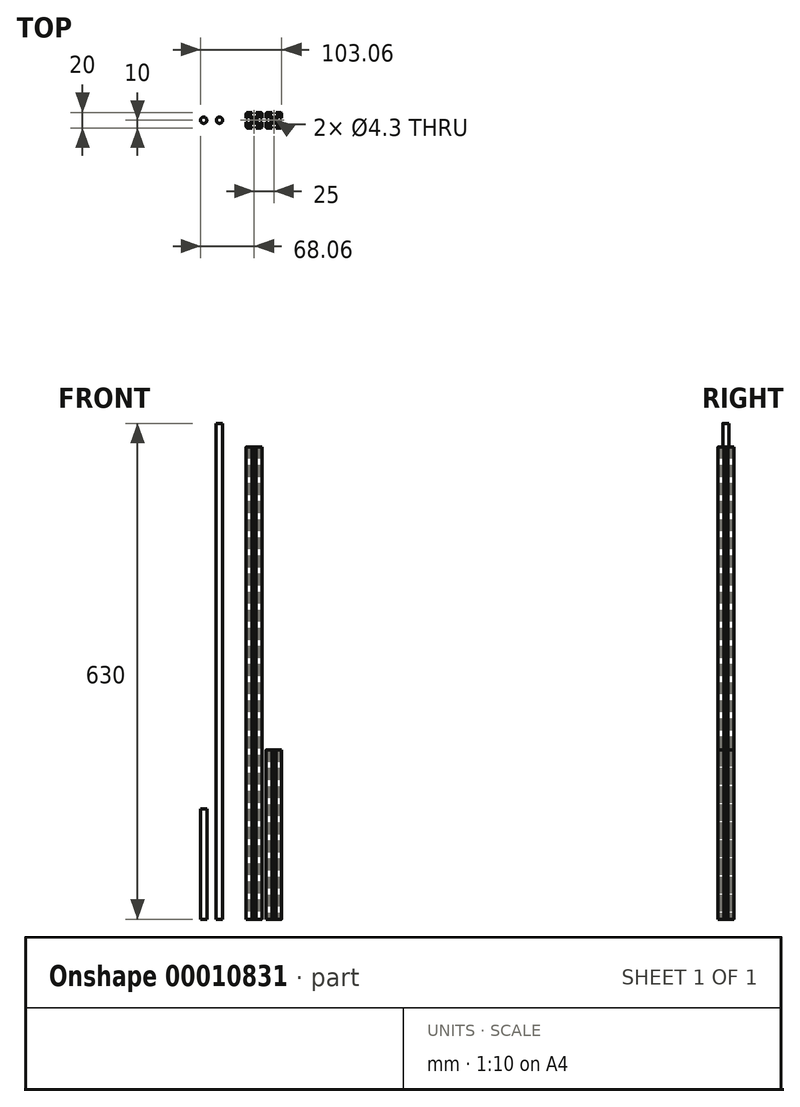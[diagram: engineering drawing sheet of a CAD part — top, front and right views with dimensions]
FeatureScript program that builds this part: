
annotation { "Feature Type Name" : "Feature", "Feature Type Description" : "" }
export const myFeature = defineFeature(function(context is Context, id is Id, definition is map)
    precondition{}
    {
        {
            var Q0;
            Q0=qCreatedBy(makeId("Top.planeOp"),FACE);
            var sketch = newSketch(context, id + "F0", { "sketchPlane" : qUnion([Q0])});
            skLineSegment(sketch, "E0.rect.bottom", {"start": v(8, 10) * mm, "end": v(-8, 10) * mm});
            skLineSegment(sketch, "E0.rect.top", {"start": v(8, -10) * mm, "end": v(-8, -10) * mm});
            skLineSegment(sketch, "E0.rect.left", {"start": v(10, 8) * mm, "end": v(10, -8) * mm});
            skLineSegment(sketch, "E0.rect.right", {"start": v(-10, 8) * mm, "end": v(-10, -8) * mm});
            skPoint(sketch, "E0.rect.middle", {"position": v(0, 0) * mm});
            skPoint(sketch, "E1.visualSharp", {"position": v(-10, 10) * mm});
            skArc(sketch, "E1.filletArc", {"start": v(-8, 10) * mm, "mid": v(-9.41, 9.41) * mm, "end": v(-10, 8) * mm});
            skPoint(sketch, "E2.visualSharp", {"position": v(10, 10) * mm});
            skArc(sketch, "E2.filletArc", {"start": v(10, 8) * mm, "mid": v(9.41, 9.41) * mm, "end": v(8, 10) * mm});
            skPoint(sketch, "E3.visualSharp", {"position": v(10, -10) * mm});
            skArc(sketch, "E3.filletArc", {"start": v(8, -10) * mm, "mid": v(9.41, -9.41) * mm, "end": v(10, -8) * mm});
            skPoint(sketch, "E4.visualSharp", {"position": v(-10, -10) * mm});
            skArc(sketch, "E4.filletArc", {"start": v(-10, -8) * mm, "mid": v(-9.41, -9.41) * mm, "end": v(-8, -10) * mm});
            skCircle(sketch, "E5", {"center": v(0, 0) * mm, "radius": 2.15 * mm});
            skCircle(sketch, "E6", {"center": v(0, 0) * mm, "radius": 3.65 * mm});
            skLineSegment(sketch, "E7", {"start": v(-2.5, 10) * mm, "end": v(-2.5, 8.2) * mm});
            skLineSegment(sketch, "E8", {"start": v(-2.5, 8.2) * mm, "end": v(-5.7, 8.2) * mm});
            skLineSegment(sketch, "E9", {"start": v(-5.7, 8.2) * mm, "end": v(-5.7, 7) * mm});
            skLineSegment(sketch, "E10", {"start": v(-5.7, 7) * mm, "end": v(-1.85, 3.15) * mm});
            skLineSegment(sketch, "E11", {"start": v(0, 16.28) * mm, "end": v(0, -16.6) * mm, "construction": true});
            skLineSegment(sketch, "E12", {"start": v(2.5, 10) * mm, "end": v(2.5, 8.2) * mm});
            skLineSegment(sketch, "E13", {"start": v(2.5, 8.2) * mm, "end": v(5.7, 8.2) * mm});
            skLineSegment(sketch, "E14", {"start": v(5.7, 8.2) * mm, "end": v(5.7, 7) * mm});
            skLineSegment(sketch, "E15", {"start": v(5.7, 7) * mm, "end": v(1.85, 3.15) * mm});
            skLineSegment(sketch, "E16.1.0", {"start": v(-7, -5.7) * mm, "end": v(-3.15, -1.85) * mm});
            skLineSegment(sketch, "E16.1.1", {"start": v(-8.2, -5.7) * mm, "end": v(-7, -5.7) * mm});
            skLineSegment(sketch, "E16.1.2", {"start": v(-8.2, -2.5) * mm, "end": v(-8.2, -5.7) * mm});
            skLineSegment(sketch, "E16.1.3", {"start": v(-10, -2.5) * mm, "end": v(-8.2, -2.5) * mm});
            skLineSegment(sketch, "E16.1.4", {"start": v(-10, 2.5) * mm, "end": v(-8.2, 2.5) * mm});
            skLineSegment(sketch, "E16.1.5", {"start": v(-8.2, 2.5) * mm, "end": v(-8.2, 5.7) * mm});
            skLineSegment(sketch, "E16.1.6", {"start": v(-8.2, 5.7) * mm, "end": v(-7, 5.7) * mm});
            skLineSegment(sketch, "E16.1.7", {"start": v(-7, 5.7) * mm, "end": v(-3.15, 1.85) * mm});
            skLineSegment(sketch, "E16.2.0", {"start": v(5.7, -7) * mm, "end": v(1.85, -3.15) * mm});
            skLineSegment(sketch, "E16.2.1", {"start": v(5.7, -8.2) * mm, "end": v(5.7, -7) * mm});
            skLineSegment(sketch, "E16.2.2", {"start": v(2.5, -8.2) * mm, "end": v(5.7, -8.2) * mm});
            skLineSegment(sketch, "E16.2.3", {"start": v(2.5, -10) * mm, "end": v(2.5, -8.2) * mm});
            skLineSegment(sketch, "E16.2.4", {"start": v(-2.5, -10) * mm, "end": v(-2.5, -8.2) * mm});
            skLineSegment(sketch, "E16.2.5", {"start": v(-2.5, -8.2) * mm, "end": v(-5.7, -8.2) * mm});
            skLineSegment(sketch, "E16.2.6", {"start": v(-5.7, -8.2) * mm, "end": v(-5.7, -7) * mm});
            skLineSegment(sketch, "E16.2.7", {"start": v(-5.7, -7) * mm, "end": v(-1.85, -3.15) * mm});
            skLineSegment(sketch, "E16.3.0", {"start": v(7, 5.7) * mm, "end": v(3.15, 1.85) * mm});
            skLineSegment(sketch, "E16.3.1", {"start": v(8.2, 5.7) * mm, "end": v(7, 5.7) * mm});
            skLineSegment(sketch, "E16.3.2", {"start": v(8.2, 2.5) * mm, "end": v(8.2, 5.7) * mm});
            skLineSegment(sketch, "E16.3.3", {"start": v(10, 2.5) * mm, "end": v(8.2, 2.5) * mm});
            skLineSegment(sketch, "E16.3.4", {"start": v(10, -2.5) * mm, "end": v(8.2, -2.5) * mm});
            skLineSegment(sketch, "E16.3.5", {"start": v(8.2, -2.5) * mm, "end": v(8.2, -5.7) * mm});
            skLineSegment(sketch, "E16.3.6", {"start": v(8.2, -5.7) * mm, "end": v(7, -5.7) * mm});
            skLineSegment(sketch, "E16.3.7", {"start": v(7, -5.7) * mm, "end": v(3.15, -1.85) * mm});
            skCircle(sketch, "E17.1.0.0", {"center": v(25, 0) * mm, "radius": 2.15 * mm});
            skCircle(sketch, "E17.1.0.1", {"center": v(25, 0) * mm, "radius": 3.65 * mm});
            skLineSegment(sketch, "E17.1.0.2", {"start": v(18, 5.7) * mm, "end": v(21.85, 1.85) * mm});
            skLineSegment(sketch, "E17.1.0.3", {"start": v(32, -5.7) * mm, "end": v(28.15, -1.85) * mm});
            skLineSegment(sketch, "E17.1.0.4", {"start": v(22.5, 10) * mm, "end": v(22.5, 8.2) * mm});
            skArc(sketch, "E17.1.0.5", {"start": v(15, -8) * mm, "mid": v(15.59, -9.41) * mm, "end": v(17, -10) * mm});
            skPoint(sketch, "E17.1.0.6", {"position": v(15, 10) * mm});
            skArc(sketch, "E17.1.0.7", {"start": v(33, -10) * mm, "mid": v(34.41, -9.41) * mm, "end": v(35, -8) * mm});
            skLineSegment(sketch, "E17.1.0.8", {"start": v(22.5, 8.2) * mm, "end": v(19.3, 8.2) * mm});
            skLineSegment(sketch, "E17.1.0.9", {"start": v(18, -5.7) * mm, "end": v(21.85, -1.85) * mm});
            skArc(sketch, "E17.1.0.10", {"start": v(35, 8) * mm, "mid": v(34.41, 9.41) * mm, "end": v(33, 10) * mm});
            skLineSegment(sketch, "E17.1.0.11", {"start": v(35, 8) * mm, "end": v(35, -8) * mm});
            skArc(sketch, "E17.1.0.12", {"start": v(17, 10) * mm, "mid": v(15.59, 9.41) * mm, "end": v(15, 8) * mm});
            skLineSegment(sketch, "E17.1.0.13", {"start": v(15, 8) * mm, "end": v(15, -8) * mm});
            skLineSegment(sketch, "E17.1.0.14", {"start": v(33, -10) * mm, "end": v(17, -10) * mm});
            skLineSegment(sketch, "E17.1.0.15", {"start": v(32, 5.7) * mm, "end": v(28.15, 1.85) * mm});
            skLineSegment(sketch, "E17.1.0.16", {"start": v(19.3, 7) * mm, "end": v(23.15, 3.15) * mm});
            skLineSegment(sketch, "E17.1.0.17", {"start": v(33, 10) * mm, "end": v(17, 10) * mm});
            skLineSegment(sketch, "E17.1.0.18", {"start": v(30.7, -7) * mm, "end": v(26.85, -3.15) * mm});
            skLineSegment(sketch, "E17.1.0.19", {"start": v(27.5, 10) * mm, "end": v(27.5, 8.2) * mm});
            skLineSegment(sketch, "E17.1.0.20", {"start": v(35, -2.5) * mm, "end": v(33.2, -2.5) * mm});
            skLineSegment(sketch, "E17.1.0.21", {"start": v(15, 2.5) * mm, "end": v(16.8, 2.5) * mm});
            skLineSegment(sketch, "E17.1.0.22", {"start": v(27.5, -8.2) * mm, "end": v(30.7, -8.2) * mm});
            skLineSegment(sketch, "E17.1.0.23", {"start": v(27.5, 8.2) * mm, "end": v(30.7, 8.2) * mm});
            skPoint(sketch, "E17.1.0.24", {"position": v(35, -10) * mm});
            skLineSegment(sketch, "E17.1.0.25", {"start": v(22.5, -8.2) * mm, "end": v(19.3, -8.2) * mm});
            skPoint(sketch, "E17.1.0.26", {"position": v(35, 10) * mm});
            skLineSegment(sketch, "E17.1.0.27", {"start": v(33.2, -2.5) * mm, "end": v(33.2, -5.7) * mm});
            skLineSegment(sketch, "E17.1.0.28", {"start": v(16.8, 2.5) * mm, "end": v(16.8, 5.7) * mm});
            skLineSegment(sketch, "E17.1.0.29", {"start": v(16.8, -2.5) * mm, "end": v(16.8, -5.7) * mm});
            skLineSegment(sketch, "E17.1.0.30", {"start": v(27.5, -10) * mm, "end": v(27.5, -8.2) * mm});
            skLineSegment(sketch, "E17.1.0.31", {"start": v(33.2, 2.5) * mm, "end": v(33.2, 5.7) * mm});
            skLineSegment(sketch, "E17.1.0.32", {"start": v(15, -2.5) * mm, "end": v(16.8, -2.5) * mm});
            skLineSegment(sketch, "E17.1.0.33", {"start": v(35, 2.5) * mm, "end": v(33.2, 2.5) * mm});
            skLineSegment(sketch, "E17.1.0.34", {"start": v(22.5, -10) * mm, "end": v(22.5, -8.2) * mm});
            skLineSegment(sketch, "E17.1.0.35", {"start": v(30.7, 7) * mm, "end": v(26.85, 3.15) * mm});
            skPoint(sketch, "E17.1.0.36", {"position": v(15, -10) * mm});
            skLineSegment(sketch, "E17.1.0.37", {"start": v(19.3, -7) * mm, "end": v(23.15, -3.15) * mm});
            skLineSegment(sketch, "E17.1.0.38", {"start": v(19.3, 8.2) * mm, "end": v(19.3, 7) * mm});
            skPoint(sketch, "E17.1.0.39", {"position": v(25, 0) * mm});
            skLineSegment(sketch, "E17.1.0.40", {"start": v(16.8, -5.7) * mm, "end": v(18, -5.7) * mm});
            skLineSegment(sketch, "E17.1.0.41", {"start": v(33.2, 5.7) * mm, "end": v(32, 5.7) * mm});
            skLineSegment(sketch, "E17.1.0.42", {"start": v(30.7, -8.2) * mm, "end": v(30.7, -7) * mm});
            skLineSegment(sketch, "E17.1.0.43", {"start": v(30.7, 8.2) * mm, "end": v(30.7, 7) * mm});
            skLineSegment(sketch, "E17.1.0.44", {"start": v(19.3, -8.2) * mm, "end": v(19.3, -7) * mm});
            skLineSegment(sketch, "E17.1.0.45", {"start": v(33.2, -5.7) * mm, "end": v(32, -5.7) * mm});
            skLineSegment(sketch, "E17.1.0.46", {"start": v(16.8, 5.7) * mm, "end": v(18, 5.7) * mm});
            skPoint(sketch, "E17.1.0.47", {"position": v(25, 0) * mm});
            skLineSegment(sketch, "E17.direction1", {"start": v(0, 0) * mm, "end": v(25, 0) * mm, "construction": true});
            skCircle(sketch, "E18", {"center": v(-44.06, 0) * mm, "radius": 4 * mm});
            skSolve(sketch);
        }
        {
            var Q0;
            {var subQ5=sQuery(id+"F0.wireOp",EDGE,"E1.filletArc");Q0=makeQuery(id+"F0.imprint","IMPRINT",FACE,{"disambiguationData":[TD([[makeQuery(id+"F0.imprint","IMPRINT",EDGE,{"derivedFrom":subQ5}),1.0]])]});}
            var Q1;
            {var subQ5=sQuery(id+"F0.wireOp",EDGE,"E2.filletArc");Q1=makeQuery(id+"F0.imprint","IMPRINT",FACE,{"disambiguationData":[TD([[makeQuery(id+"F0.imprint","IMPRINT",EDGE,{"derivedFrom":subQ5}),1.0]])]});}
            var Q2;
            {var subQ4=sQuery(id+"F0.wireOp",EDGE,"E3.filletArc");Q2=makeQuery(id+"F0.imprint","IMPRINT",FACE,{"disambiguationData":[TD([[makeQuery(id+"F0.imprint","IMPRINT",EDGE,{"derivedFrom":subQ4}),1.0]])]});}
            var Q3;
            Q3=makeQuery(id+"F0.imprint","IMPRINT",FACE,{"disambiguationData":[TD([[makeQuery(id+"F0.imprint","IMPRINT",EDGE,{"derivedFrom":sQuery(id+"F0.wireOp",EDGE,"E5")}),-1.0]])]});
            var Q4;
            {var subQ5=sQuery(id+"F0.wireOp",EDGE,"E4.filletArc");Q4=makeQuery(id+"F0.imprint","IMPRINT",FACE,{"disambiguationData":[TD([[makeQuery(id+"F0.imprint","IMPRINT",EDGE,{"derivedFrom":subQ5}),1.0]])]});}
            extrude(context, id + "F1", {"entities" : qUnion([Q0, Q1, Q2, Q3, Q4]), "depth" : 600 * mm});
        }
        {
            var Q0;
            {var subQ6=sQuery(id+"F0.wireOp",EDGE,"E17.1.0.2");Q0=makeQuery(id+"F0.imprint","IMPRINT",FACE,{"disambiguationData":[TD([[makeQuery(id+"F0.imprint","IMPRINT",EDGE,{"derivedFrom":subQ6}),1.0]])]});}
            var Q1;
            {var subQ4=sQuery(id+"F0.wireOp",EDGE,"E17.1.0.10");Q1=makeQuery(id+"F0.imprint","IMPRINT",FACE,{"disambiguationData":[TD([[makeQuery(id+"F0.imprint","IMPRINT",EDGE,{"derivedFrom":subQ4}),1.0]])]});}
            var Q2;
            Q2=makeQuery(id+"F0.imprint","IMPRINT",FACE,{"disambiguationData":[TD([[makeQuery(id+"F0.imprint","IMPRINT",EDGE,{"derivedFrom":sQuery(id+"F0.wireOp",EDGE,"E17.1.0.0")}),-1.0]])]});
            var Q3;
            {var subQ6=sQuery(id+"F0.wireOp",EDGE,"E17.1.0.3");Q3=makeQuery(id+"F0.imprint","IMPRINT",FACE,{"disambiguationData":[TD([[makeQuery(id+"F0.imprint","IMPRINT",EDGE,{"derivedFrom":subQ6}),1.0]])]});}
            var Q4;
            {var subQ4=sQuery(id+"F0.wireOp",EDGE,"E17.1.0.5");Q4=makeQuery(id+"F0.imprint","IMPRINT",FACE,{"disambiguationData":[TD([[makeQuery(id+"F0.imprint","IMPRINT",EDGE,{"derivedFrom":subQ4}),1.0]])]});}
            extrude(context, id + "F2", {"entities" : qUnion([Q0, Q1, Q2, Q3, Q4]), "depth" : 215 * mm});
        }
        {
            var Q0;
            Q0=makeQuery(id+"F0.imprint","IMPRINT",FACE,{"disambiguationData":[TD([[makeQuery(id+"F0.imprint","IMPRINT",EDGE,{"derivedFrom":sQuery(id+"F0.wireOp",EDGE,"E18")}),1.0]])]});
            extrude(context, id + "F3", {"entities" : qUnion([Q0]), "depth" : 630 * mm});
        }
        {
            var Q0;
            Q0=makeQuery(id+"F3.opExtrude","SWEPT_BODY",BODY,{"disambiguationData":[OSD([sQuery(id+"F0.wireOp",EDGE,"E18")])]});
            transform(context, id + "F4", {"entities" : qUnion([Q0]), "transformType" : TransformType.TRANSLATION_3D, "dx" : -20 * mm, "dy" : 0 * mm, "dz" : 0 * mm, "makeCopy" : true});
        }
        {
            var Q0;
            Q0=makeQuery(id+"F4.opPattern","COPY",FACE,{"derivedFrom":makeQuery(id+"F3.opExtrude","CAP_FACE",FACE,{"disambiguationData":[OSD([sQuery(id+"F0.wireOp",EDGE,"E18")])],"isStart":false}),"instanceName":"1"});
            extrude(context, id + "F5", {"entities" : qUnion([Q0]), "operationType" : NewBodyOperationType.REMOVE, "oppositeDirection" : true, "depth" : 490 * mm});
        }
    });
